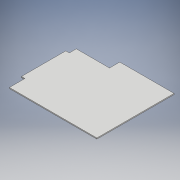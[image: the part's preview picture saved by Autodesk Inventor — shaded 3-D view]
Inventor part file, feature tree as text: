
AUTODESK INVENTOR PART (.ipt)
format: ipt  version: 2018 (Build 220112000, 112)  size: 102,912 bytes
history: native  units: mm
features: other x1, extrude x1
ambient origin geometry x8: Origin, YZ Plane, XZ Plane, XY Plane, X Axis, Y Axis, Z Axis, Center Point
bodies: Body1 (feature_tree)
feature tree (2):
  other  "ソリッド1"
  extrude  "押し出し1"  Depth=211.0mm
